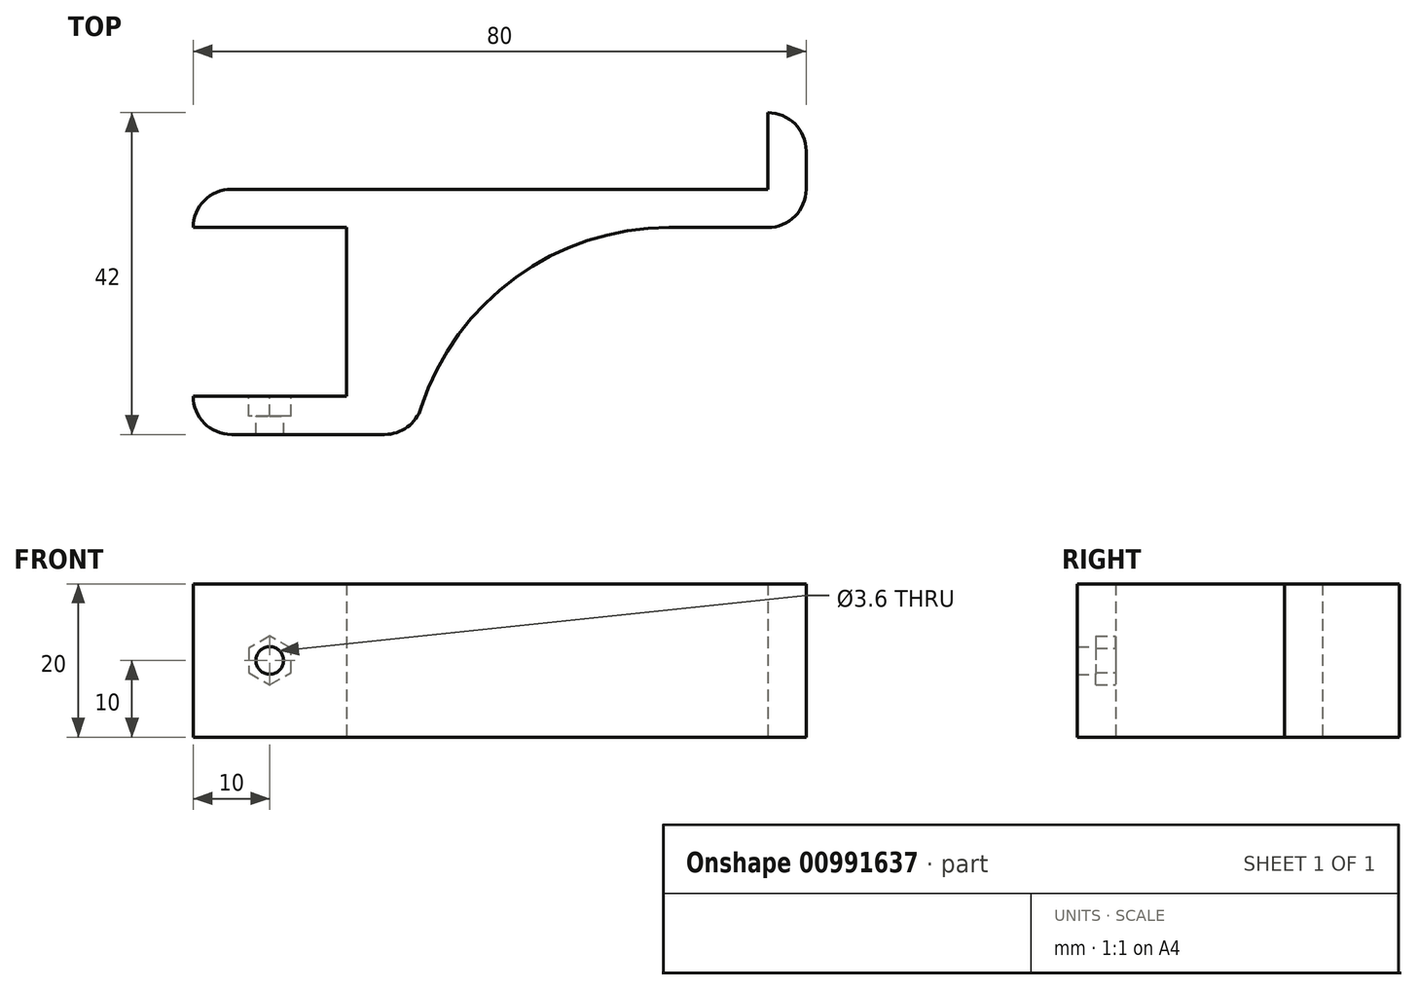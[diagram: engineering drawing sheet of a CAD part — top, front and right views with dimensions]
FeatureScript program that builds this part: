
annotation { "Feature Type Name" : "Feature", "Feature Type Description" : "" }
export const myFeature = defineFeature(function(context is Context, id is Id, definition is map)
    precondition{}
    {
        {
            assignVariable(context, id + "F0", {"name" : "BracketWidth", "anyValue" : 20});
        }
        {
            assignVariable(context, id + "F1", {"name" : "WallThickness", "anyValue" : 5});
        }
        {
            var Q0;
            Q0=qCreatedBy(makeId("Top.planeOp"),FACE);
            var sketch = newSketch(context, id + "F2", { "sketchPlane" : qUnion([Q0])});
            skLineSegment(sketch, "E0", {"start": v(0, 0) * mm, "end": v(20, 0) * mm});
            skLineSegment(sketch, "E1", {"start": v(20, 0) * mm, "end": v(20, -22) * mm});
            skLineSegment(sketch, "E2", {"start": v(20, -22) * mm, "end": v(0, -22) * mm});
            skLineSegment(sketch, "E3", {"start": v(0, -22) * mm, "end": v(0, -27) * mm});
            skLineSegment(sketch, "E4", {"start": v(0, -27) * mm, "end": v(30, -27) * mm});
            skLineSegment(sketch, "E5", {"start": v(30, -27) * mm, "end": v(30, 0) * mm});
            skLineSegment(sketch, "E6", {"start": v(30, 0) * mm, "end": v(80, 0) * mm});
            skLineSegment(sketch, "E7", {"start": v(80, 0) * mm, "end": v(80, 15) * mm});
            skLineSegment(sketch, "E8", {"start": v(80, 15) * mm, "end": v(75, 15) * mm});
            skLineSegment(sketch, "E9", {"start": v(75, 15) * mm, "end": v(75, 5) * mm});
            skLineSegment(sketch, "E10", {"start": v(75, 5) * mm, "end": v(0, 5) * mm});
            skLineSegment(sketch, "E11", {"start": v(0, 5) * mm, "end": v(0, 0) * mm});
            skSolve(sketch);
        }
        {
            var Q0;
            Q0=qSketchRegion(id+"F2",true);
            extrude(context, id + "F3", {"entities" : qUnion([Q0]), "depth" : (getVariable(context, 'BracketWidth')) * mm, "offsetDistance" : 25 * mm});
        }
        {
            var Q0;
            Q0=makeQuery(id+"F3.opExtrude","SWEPT_EDGE",EDGE,{"disambiguationData":[OSD([sQuery(id+"F2.wireOp",EDGE,"E4"),sQuery(id+"F2.wireOp",EDGE,"E5")])]});
            var Q1;
            Q1=makeQuery(id+"F3.opExtrude","SWEPT_EDGE",EDGE,{"disambiguationData":[OSD([sQuery(id+"F2.wireOp",EDGE,"E6"),sQuery(id+"F2.wireOp",EDGE,"E7")])]});
            var Q2;
            Q2=makeQuery(id+"F3.opExtrude","SWEPT_EDGE",EDGE,{"disambiguationData":[OSD([sQuery(id+"F2.wireOp",EDGE,"E7"),sQuery(id+"F2.wireOp",EDGE,"E8")])]});
            var Q3;
            Q3=makeQuery(id+"F3.opExtrude","SWEPT_EDGE",EDGE,{"disambiguationData":[OSD([sQuery(id+"F2.wireOp",EDGE,"E10"),sQuery(id+"F2.wireOp",EDGE,"E11")])]});
            var Q4;
            Q4=makeQuery(id+"F3.opExtrude","SWEPT_EDGE",EDGE,{"disambiguationData":[OSD([sQuery(id+"F2.wireOp",EDGE,"E3"),sQuery(id+"F2.wireOp",EDGE,"E4")])]});
            fillet(context, id + "F4", {"entities" : qUnion([Q0, Q1, Q2, Q3, Q4]), "radius" : (getVariable(context, 'WallThickness')) * mm, "tangentPropagation" : true, "defaultsChanged" : false, "vertexSettings" : [], "allowEdgeOverflow" : false});
        }
        {
            var Q0;
            Q0=makeQuery(id+"F3.opExtrude","SWEPT_FACE",FACE,{"disambiguationData":[OSD([sQuery(id+"F2.wireOp",EDGE,"E2")])]});
            var sketch = newSketch(context, id + "F5", { "sketchPlane" : qUnion([Q0])});
            skLineSegment(sketch, "E12", {"start": v(0, 20) * mm, "end": v(-20, 0) * mm, "construction": true});
            skLineSegment(sketch, "E13", {"start": v(-20, 0) * mm, "end": v(0, 0) * mm, "construction": true});
            skLineSegment(sketch, "E14", {"start": v(0, 0) * mm, "end": v(-20, 20) * mm, "construction": true});
            skLineSegment(sketch, "E15", {"start": v(-20, 20) * mm, "end": v(0, 20) * mm, "construction": true});
            skPoint(sketch, "E16", {"position": v(-10, 10) * mm});
            skCircle(sketch, "E17.cCircle", {"center": v(-10, 10) * mm, "radius": 2.75 * mm, "construction": true});
            skLineSegment(sketch, "E17.0", {"start": v(-7.25, 11.59) * mm, "end": v(-7.25, 8.41) * mm});
            skLineSegment(sketch, "E17.1", {"start": v(-7.25, 8.41) * mm, "end": v(-10, 6.82) * mm});
            skLineSegment(sketch, "E17.2", {"start": v(-10, 6.82) * mm, "end": v(-12.75, 8.41) * mm});
            skLineSegment(sketch, "E17.3", {"start": v(-12.75, 8.41) * mm, "end": v(-12.75, 11.59) * mm});
            skLineSegment(sketch, "E17.4", {"start": v(-12.75, 11.59) * mm, "end": v(-10, 13.18) * mm});
            skLineSegment(sketch, "E17.5", {"start": v(-10, 13.18) * mm, "end": v(-7.25, 11.59) * mm});
            skPoint(sketch, "E17.0.midPoint", {"position": v(-7.25, 10) * mm});
            skSolve(sketch);
        }
        {
            var Q0;
            Q0=qSketchRegion(id+"F5",true);
            extrude(context, id + "F6", {"entities" : qUnion([Q0]), "operationType" : NewBodyOperationType.REMOVE, "oppositeDirection" : true, "depth" : 2.6 * mm, "offsetDistance" : 25 * mm});
        }
        {
            var Q0;
            Q0=sQuery(id+"F5.wireOp",VERTEX,"E16");
            var Q1;
            Q1=makeQuery(id+"F3.opExtrude","SWEPT_BODY",BODY,{"disambiguationData":[OSD([sQuery(id+"F2.wireOp",EDGE,"E0"),sQuery(id+"F2.wireOp",EDGE,"E1"),sQuery(id+"F2.wireOp",EDGE,"E2"),sQuery(id+"F2.wireOp",EDGE,"E3"),sQuery(id+"F2.wireOp",EDGE,"E4"),sQuery(id+"F2.wireOp",EDGE,"E5"),sQuery(id+"F2.wireOp",EDGE,"E6"),sQuery(id+"F2.wireOp",EDGE,"E7"),sQuery(id+"F2.wireOp",EDGE,"E8"),sQuery(id+"F2.wireOp",EDGE,"E9"),sQuery(id+"F2.wireOp",EDGE,"E10"),sQuery(id+"F2.wireOp",EDGE,"E11")])]});
            hole(context, id + "F7", {"style" : HoleStyle.SIMPLE, "endStyle" : HoleEndStyle.BLIND, "standardTappedOrClearance" : lookupTablePath({ "fit" : "Loose", "standard" : "ISO", "size" : "M3", "type" : "Clearance" }), "standardBlindInLast" : lookupTablePath({ "fit" : "Loose", "standard" : "ISO", "engagement" : "75%", "pitch" : "0.5 mm", "size" : "M3", "type" : "Clearance & tapped" }), "holeDiameter" : 3.6 * mm, "majorDiameter" : 5 * mm, "holeDepth" : 10 * mm, "isTappedThrough" : true, "tappedDepth" : 12 * mm, "tapClearance" : 3, "startFromSketch" : true, "locations" : qUnion([Q0]), "scope" : qUnion([Q1])});
        }
        {
            var Q0;
            Q0=makeQuery(id+"F3.opExtrude","SWEPT_EDGE",EDGE,{"disambiguationData":[OSD([sQuery(id+"F2.wireOp",EDGE,"E5"),sQuery(id+"F2.wireOp",EDGE,"E6")])]});
            fillet(context, id + "F8", {"entities" : qUnion([Q0]), "tangentPropagation" : true, "radius" : 34 * mm, "defaultsChanged" : true, "vertexSettings" : [], "allowEdgeOverflow" : false});
        }
    });
